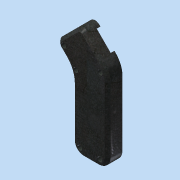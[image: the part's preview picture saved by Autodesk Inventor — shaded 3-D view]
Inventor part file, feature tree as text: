
AUTODESK INVENTOR PART (.ipt)
format: ipt  version: 2015 (Build 190159000, 159)  size: 210,432 bytes
history: native  units: in
note: dims shown in document units (in); Inventor stores cm internally (conversion verified against a paired STEP export)
features: other x3, sketch x3, extrude x2
ambient origin geometry x8: Origin, YZ Plane, XZ Plane, XY Plane, X Axis, Y Axis, Z Axis, Center Point
bodies: Solid1 (feature_tree)
feature tree (8):
  other  "CaseRight.ipt"
  extrude  "Extrusion1"  Depth=0.125in TaperAngle=0.0deg
  extrude  "Extrusion2"  Depth=0.0312in TaperAngle=0.0deg
  other  "Solid1::CaseRight.ipt"
  other  "TaggingFeature1"
  sketch  "Sketch3"  dims[d4=0.0312in d5=0.0312in d6=0.0in]
  sketch  "Sketch2"  dims[d0=0.3937in d1=0.125in d2=0.0in]
  sketch  "Sketch4"
